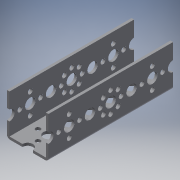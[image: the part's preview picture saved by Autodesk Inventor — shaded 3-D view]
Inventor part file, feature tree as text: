
AUTODESK INVENTOR PART (.ipt)
format: ipt  version: 2019 (Build 230136000, 136)  size: 438,272 bytes
history: native  units: in
note: dims shown in document units (in); Inventor stores cm internally (conversion verified against a paired STEP export)
features: other x1, imported_body x1, move_body x1, plane x1, extrude x1, sketch x1
ambient origin geometry x8: Origin, YZ Plane, XZ Plane, XY Plane, X Axis, Y Axis, Z Axis, Center Point
bodies: Body1 (feature_tree)
feature tree (6):
  other  "CHANNEL_288_2011"
  imported_body  "Base1"
  move_body  "Move Body1"
  plane  "Work Plane3"
  extrude  "Extrusion1"  Depth=0.3937in
  sketch  "Sketch2"  dims[d1=0.0in d2=0.0in d3=5.0394in d4=1.378in d5=0.0in d6=0.3937in d7=0.0in]
